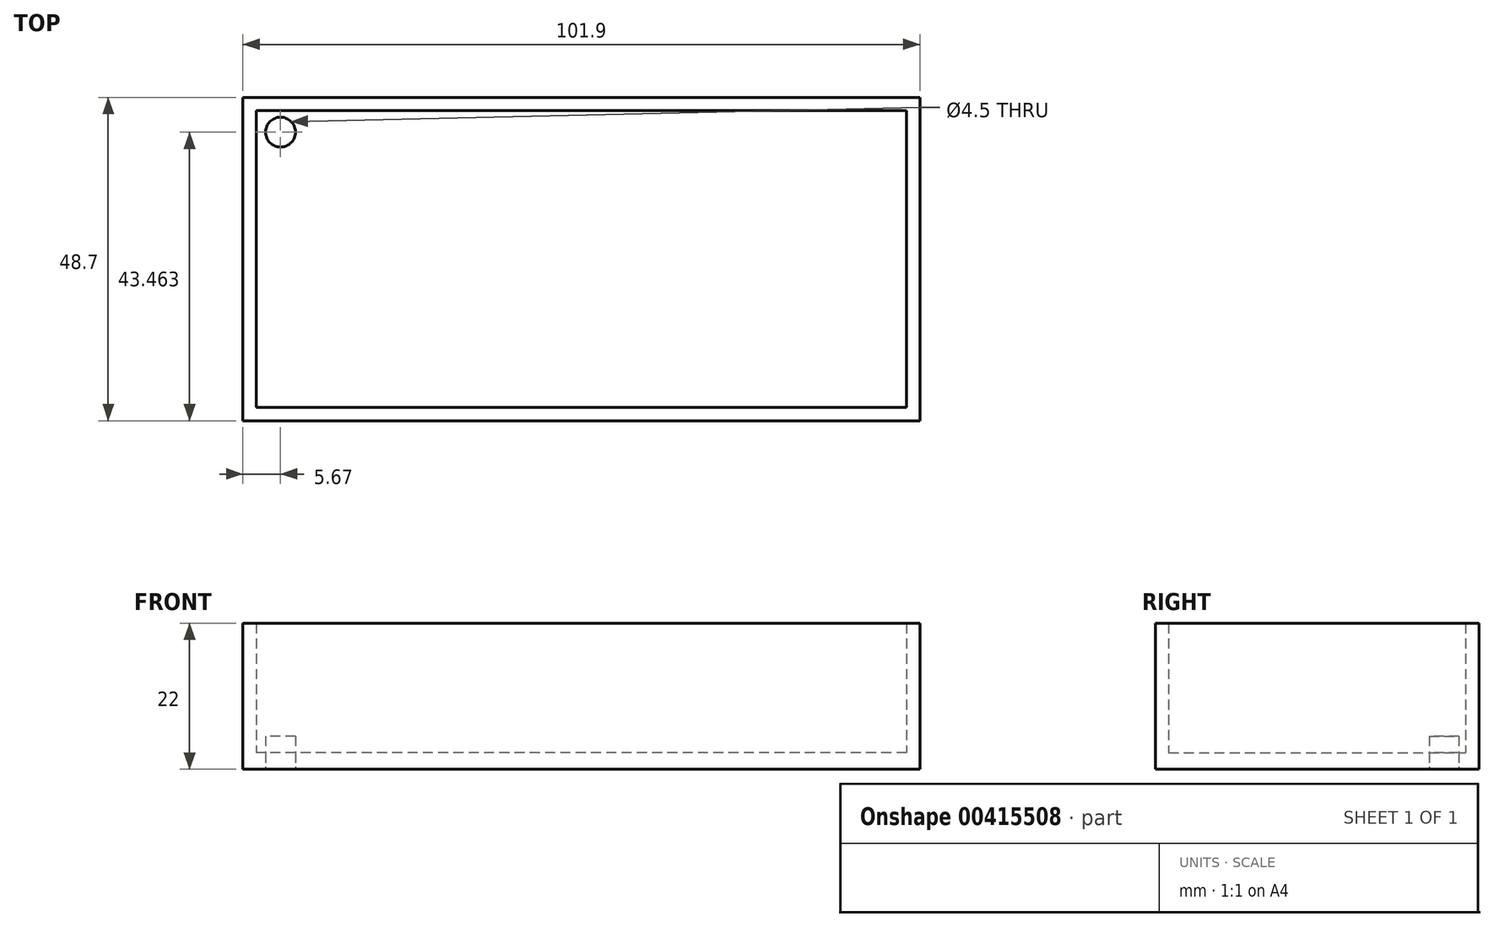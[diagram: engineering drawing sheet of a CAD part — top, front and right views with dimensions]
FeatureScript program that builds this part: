
annotation { "Feature Type Name" : "Feature", "Feature Type Description" : "" }
export const myFeature = defineFeature(function(context is Context, id is Id, definition is map)
    precondition{}
    {
        {
            var Q0;
            Q0=qCreatedBy(makeId("Top.planeOp"),FACE);
            var sketch = newSketch(context, id + "F0", { "sketchPlane" : qUnion([Q0])});
            skLineSegment(sketch, "E0.bottom", {"start": v(26.55, -22.35) * mm, "end": v(-26.55, -22.35) * mm});
            skLineSegment(sketch, "E0.top", {"start": v(26.55, 22.35) * mm, "end": v(-26.55, 22.35) * mm});
            skLineSegment(sketch, "E0.left", {"start": v(26.55, -22.35) * mm, "end": v(26.55, 22.35) * mm});
            skLineSegment(sketch, "E0.right", {"start": v(-26.55, -22.35) * mm, "end": v(-26.55, 22.35) * mm});
            skPoint(sketch, "E0.middle", {"position": v(0, 0) * mm});
            skCircle(sketch, "E1", {"center": v(-22.88, 19.11) * mm, "radius": 2.25 * mm});
            skSolve(sketch);
        }
        {
            var Q0;
            Q0=makeQuery(id+"F0.imprint","IMPRINT",FACE,{"disambiguationData":[TD([[makeQuery(id+"F0.imprint","IMPRINT",EDGE,{"derivedFrom":sQuery(id+"F0.wireOp",EDGE,"42514434-9cf8-42b0-99da-e163298d3522")}),1.0]])]});
            var Q1;
            Q1=makeQuery(id+"F0.imprint","IMPRINT",FACE,{"disambiguationData":[TD([[makeQuery(id+"F0.imprint","IMPRINT",EDGE,{"derivedFrom":sQuery(id+"F0.wireOp",EDGE,"E1")}),1.0]])]});
            var Q2;
            Q2=makeQuery(id+"F0.imprint","IMPRINT",FACE,{"disambiguationData":[TD([[makeQuery(id+"F0.imprint","IMPRINT",EDGE,{"derivedFrom":sQuery(id+"F0.wireOp",EDGE,"803385ed-862d-41f7-99c5-e472b14c8cbd")}),1.0]])]});
            var Q3;
            Q3=makeQuery(id+"F0.imprint","IMPRINT",FACE,{"disambiguationData":[TD([[makeQuery(id+"F0.imprint","IMPRINT",EDGE,{"derivedFrom":sQuery(id+"F0.wireOp",EDGE,"c87ae84e-c973-458d-bcb9-c45d14dc737d")}),1.0]])]});
            extrude(context, id + "F1", {"entities" : qUnion([Q0, Q1, Q2, Q3]), "depth" : 5 * mm});
        }
        {
            var Q0;
            Q0=makeQuery(id+"F0.imprint","IMPRINT",FACE,{"disambiguationData":[TD([[makeQuery(id+"F0.imprint","IMPRINT",EDGE,{"derivedFrom":sQuery(id+"F0.wireOp",EDGE,"E0.bottom")}),-1.0]])]});
            extrude(context, id + "F2", {"entities" : qUnion([Q0]), "depth" : 2.5 * mm});
        }
        {
            var Q0;
            Q0=makeQuery(id+"F1.opExtrude","CAP_FACE",FACE,{"disambiguationData":[OSD([sQuery(id+"F0.wireOp",EDGE,"E1")])],"isStart":false});
            var sketch = newSketch(context, id + "F3", { "sketchPlane" : qUnion([Q0])});
            skSolve(sketch);
        }
        {
            var Q0;
            Q0=makeQuery(id+"F3.imprint","IMPRINT",FACE,{"disambiguationData":[TD([[makeQuery(id+"F3.imprint","IMPRINT",EDGE,{"derivedFrom":makeQuery(id+"F1.opExtrude","CAP_EDGE",EDGE,{"disambiguationData":[OSD([sQuery(id+"F0.wireOp",EDGE,"E1")])],"isStart":false})}),1.0]])]});
            var sketch = newSketch(context, id + "F4", { "sketchPlane" : qUnion([Q0])});
            skCircle(sketch, "E2", {"center": v(-24.05, 19.95) * mm, "radius": 1.25 * mm});
            skCircle(sketch, "E3", {"center": v(-24.18, -19.73) * mm, "radius": 1.25 * mm});
            skCircle(sketch, "E4", {"center": v(24.02, -19.72) * mm, "radius": 1.25 * mm});
            skCircle(sketch, "E5", {"center": v(24.14, 19.9) * mm, "radius": 1.25 * mm});
            skSolve(sketch);
        }
        {
            var Q0;
            Q0=sQuery(id+"F4.wireOp",EDGE,"E3");
            var Q1;
            Q1=sQuery(id+"F4.wireOp",EDGE,"E2");
            var Q2;
            Q2=sQuery(id+"F4.wireOp",EDGE,"E5");
            var Q3;
            Q3=sQuery(id+"F4.wireOp",EDGE,"E4");
            extrude(context, id + "F5", {"bodyType" : ToolBodyType.SURFACE, "surfaceEntities" : qUnion([Q0, Q1, Q2, Q3]), "depth" : 3 * mm});
        }
        {
            var Q0;
            Q0=makeQuery(id+"F2.opExtrude","SWEPT_FACE",FACE,{"disambiguationData":[OSD([sQuery(id+"F0.wireOp",EDGE,"E0.left")])]});
            extrude(context, id + "F6", {"entities" : qUnion([Q0]), "operationType" : NewBodyOperationType.ADD, "depth" : 44.8 * mm});
        }
        {
            var Q0;
            Q0=qCreatedBy(makeId("Top.planeOp"),FACE);
            var sketch = newSketch(context, id + "F7", { "sketchPlane" : qUnion([Q0])});
            skLineSegment(sketch, "E6.0", {"start": v(71.35, 22.35) * mm, "end": v(-26.55, 22.35) * mm});
            skLineSegment(sketch, "E7.0", {"start": v(71.35, -22.35) * mm, "end": v(71.35, 22.35) * mm});
            skLineSegment(sketch, "E8.0", {"start": v(71.35, -22.35) * mm, "end": v(-26.55, -22.35) * mm});
            skLineSegment(sketch, "E9.0", {"start": v(-26.55, -22.35) * mm, "end": v(-26.55, 22.35) * mm});
            skLineSegment(sketch, "E10.0.0", {"start": v(-26.55, -22.35) * mm, "end": v(71.35, -22.35) * mm});
            skLineSegment(sketch, "E10.0.3", {"start": v(-26.55, 22.35) * mm, "end": v(-26.55, -22.35) * mm});
            skLineSegment(sketch, "E11.bottom", {"start": v(-26.55, 22.35) * mm, "end": v(71.35, 22.35) * mm});
            skLineSegment(sketch, "E11.right", {"start": v(71.35, 22.35) * mm, "end": v(71.35, -22.35) * mm});
            skLineSegment(sketch, "E12.0", {"start": v(73.35, -24.35) * mm, "end": v(-28.55, -24.35) * mm});
            skLineSegment(sketch, "E12.1", {"start": v(73.35, -24.35) * mm, "end": v(73.35, 24.35) * mm});
            skLineSegment(sketch, "E12.2", {"start": v(73.35, 24.35) * mm, "end": v(-28.55, 24.35) * mm});
            skLineSegment(sketch, "E12.3", {"start": v(-28.55, 24.35) * mm, "end": v(-28.55, -24.35) * mm});
            skSolve(sketch);
        }
        {
            var Q0;
            Q0 = qSketchRegion(id + "F7", true);
            extrude(context, id + "F8", {"entities" : qUnion([Q0]), "operationType" : NewBodyOperationType.ADD, "depth" : 22 * mm});
        }
    });
